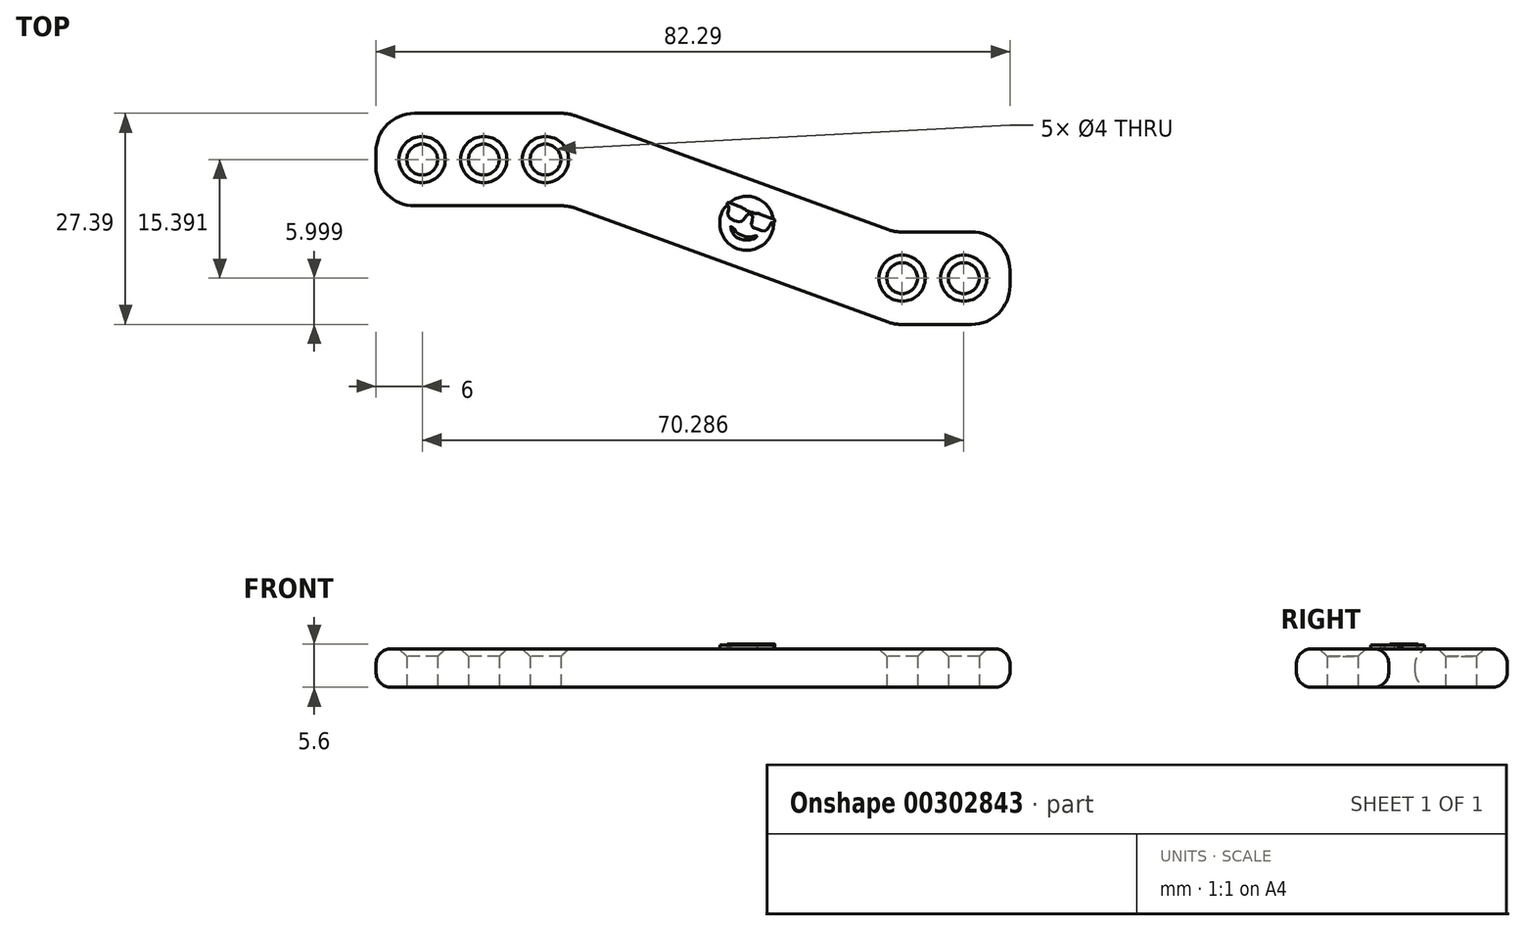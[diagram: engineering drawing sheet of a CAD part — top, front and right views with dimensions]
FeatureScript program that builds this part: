
annotation { "Feature Type Name" : "Feature", "Feature Type Description" : "" }
export const myFeature = defineFeature(function(context is Context, id is Id, definition is map)
    precondition{}
    {
        {
            var Q0;
            Q0=qCreatedBy(makeId("Top.planeOp"),FACE);
            var sketch = newSketch(context, id + "F0", { "sketchPlane" : qUnion([Q0])});
            skLineSegment(sketch, "E0.bottom", {"start": v(0, 0) * mm, "end": v(25, 0) * mm});
            skLineSegment(sketch, "E0.top", {"start": v(0, 12) * mm, "end": v(25, 12) * mm});
            skLineSegment(sketch, "E0.left", {"start": v(0, 0) * mm, "end": v(0, 12) * mm});
            skLineSegment(sketch, "E0.right", {"start": v(25, 0) * mm, "end": v(25, 12) * mm});
            skLineSegment(sketch, "E1", {"start": v(25, 12) * mm, "end": v(67.29, -3.4) * mm});
            skLineSegment(sketch, "E2", {"start": v(25, 0) * mm, "end": v(67.29, -15.4) * mm});
            skLineSegment(sketch, "E3", {"start": v(67.29, -3.4) * mm, "end": v(67.29, -15.4) * mm});
            skLineSegment(sketch, "E4.bottom", {"start": v(67.29, -3.4) * mm, "end": v(82.29, -3.4) * mm});
            skLineSegment(sketch, "E4.top", {"start": v(67.29, -15.4) * mm, "end": v(82.29, -15.4) * mm});
            skLineSegment(sketch, "E4.right", {"start": v(82.29, -3.4) * mm, "end": v(82.29, -15.4) * mm});
            skSolve(sketch);
        }
        {
            var Q0;
            Q0=makeQuery(id+"F0.imprint","IMPRINT",FACE,{"disambiguationData":[TD([[makeQuery(id+"F0.imprint","IMPRINT",EDGE,{"derivedFrom":sQuery(id+"F0.wireOp",EDGE,"E0.bottom")}),1.0]])]});
            var Q1;
            Q1=makeQuery(id+"F0.imprint","IMPRINT",FACE,{"disambiguationData":[TD([[makeQuery(id+"F0.imprint","IMPRINT",EDGE,{"derivedFrom":sQuery(id+"F0.wireOp",EDGE,"E0.right")}),-1.0]])]});
            var Q2;
            Q2=makeQuery(id+"F0.imprint","IMPRINT",FACE,{"disambiguationData":[TD([[makeQuery(id+"F0.imprint","IMPRINT",EDGE,{"derivedFrom":sQuery(id+"F0.wireOp",EDGE,"E4.bottom")}),-1.0]])]});
            extrude(context, id + "F1", {"entities" : qUnion([Q0, Q1, Q2]), "depth" : 5 * mm});
        }
        {
            var Q0;
            Q0=qCreatedBy(makeId("Top.planeOp"),FACE);
            var sketch = newSketch(context, id + "F2", { "sketchPlane" : qUnion([Q0])});
            skCircle(sketch, "E5", {"center": v(6, 6) * mm, "radius": 2 * mm});
            skCircle(sketch, "E6", {"center": v(76.29, -9.4) * mm, "radius": 2 * mm});
            skCircle(sketch, "E7.1.0.0", {"center": v(14, 6) * mm, "radius": 2 * mm});
            skCircle(sketch, "E7.2.0.0", {"center": v(22, 6) * mm, "radius": 2 * mm});
            skLineSegment(sketch, "E7.direction1", {"start": v(6, 6) * mm, "end": v(14, 6) * mm, "construction": true});
            skCircle(sketch, "E8.1.0.0", {"center": v(68.29, -9.4) * mm, "radius": 2 * mm});
            skLineSegment(sketch, "E8.direction1", {"start": v(76.29, -9.4) * mm, "end": v(68.29, -9.4) * mm, "construction": true});
            skSolve(sketch);
        }
        {
            var Q0;
            Q0 = qSketchRegion(id + "F2", true);
            extrude(context, id + "F3", {"entities" : qUnion([Q0]), "operationType" : NewBodyOperationType.REMOVE, "endBound" : BoundingType.THROUGH_ALL, "depth" : 25 * mm});
        }
        {
            var Q0;
            Q0=makeQuery(id+"F1.opExtrude","SWEPT_EDGE",EDGE,{"disambiguationData":[OSD([sQuery(id+"F0.wireOp",EDGE,"E0.top"),sQuery(id+"F0.wireOp",EDGE,"E0.left")])]});
            var Q1;
            Q1=makeQuery(id+"F1.opExtrude","SWEPT_EDGE",EDGE,{"disambiguationData":[OSD([sQuery(id+"F0.wireOp",EDGE,"E0.bottom"),sQuery(id+"F0.wireOp",EDGE,"E0.left")])]});
            var Q2;
            Q2=makeQuery(id+"F1.opExtrude","SWEPT_EDGE",EDGE,{"disambiguationData":[OSD([sQuery(id+"F0.wireOp",EDGE,"E4.bottom"),sQuery(id+"F0.wireOp",EDGE,"E4.right")])]});
            var Q3;
            Q3=makeQuery(id+"F1.opExtrude","SWEPT_EDGE",EDGE,{"disambiguationData":[OSD([sQuery(id+"F0.wireOp",EDGE,"E4.top"),sQuery(id+"F0.wireOp",EDGE,"E4.right")])]});
            var Q4;
            Q4=makeQuery(id+"F1.opExtrude","SWEPT_EDGE",EDGE,{"disambiguationData":[OSD([sQuery(id+"F0.wireOp",EDGE,"E0.top"),sQuery(id+"F0.wireOp",EDGE,"E0.right"),sQuery(id+"F0.wireOp",EDGE,"E1")])]});
            var Q5;
            Q5=makeQuery(id+"F1.opExtrude","SWEPT_EDGE",EDGE,{"disambiguationData":[OSD([sQuery(id+"F0.wireOp",EDGE,"E1"),sQuery(id+"F0.wireOp",EDGE,"E4.bottom"),sQuery(id+"F0.wireOp",EDGE,"E3")])]});
            var Q6;
            Q6=makeQuery(id+"F1.opExtrude","SWEPT_EDGE",EDGE,{"disambiguationData":[OSD([sQuery(id+"F0.wireOp",EDGE,"E2"),sQuery(id+"F0.wireOp",EDGE,"E4.top"),sQuery(id+"F0.wireOp",EDGE,"E3")])]});
            var Q7;
            Q7=makeQuery(id+"F1.opExtrude","SWEPT_EDGE",EDGE,{"disambiguationData":[OSD([sQuery(id+"F0.wireOp",EDGE,"E0.bottom"),sQuery(id+"F0.wireOp",EDGE,"E0.right"),sQuery(id+"F0.wireOp",EDGE,"E2")])]});
            fillet(context, id + "F4", {"entities" : qUnion([Q0, Q1, Q2, Q3, Q4, Q5, Q6, Q7]), "radius" : 5 * mm, "tangentPropagation" : true, "allowEdgeOverflow" : false});
        }
        {
            var Q0;
            Q0=makeQuery(id+"F1.opExtrude","CAP_EDGE",EDGE,{"disambiguationData":[OSD([sQuery(id+"F0.wireOp",EDGE,"E0.top")])],"isStart":false});
            var Q1;
            Q1=makeQuery(id+"F1.opExtrude","CAP_EDGE",EDGE,{"disambiguationData":[OSD([sQuery(id+"F0.wireOp",EDGE,"E0.bottom")])],"isStart":false});
            var Q2;
            Q2=makeQuery(id+"F1.opExtrude","CAP_EDGE",EDGE,{"disambiguationData":[OSD([sQuery(id+"F0.wireOp",EDGE,"E0.top")])],"isStart":true});
            var Q3;
            Q3=makeQuery(id+"F1.opExtrude","CAP_EDGE",EDGE,{"disambiguationData":[OSD([sQuery(id+"F0.wireOp",EDGE,"E0.bottom")])],"isStart":true});
            var Q4;
            Q4=makeQuery(id+"F1.opExtrude","CAP_EDGE",EDGE,{"disambiguationData":[OSD([sQuery(id+"F0.wireOp",EDGE,"E4.bottom")])],"isStart":false});
            var Q5;
            Q5=makeQuery(id+"F1.opExtrude","CAP_EDGE",EDGE,{"disambiguationData":[OSD([sQuery(id+"F0.wireOp",EDGE,"E4.top")])],"isStart":false});
            var Q6;
            Q6=makeQuery(id+"F1.opExtrude","CAP_EDGE",EDGE,{"disambiguationData":[OSD([sQuery(id+"F0.wireOp",EDGE,"E4.bottom")])],"isStart":true});
            var Q7;
            Q7=makeQuery(id+"F1.opExtrude","CAP_EDGE",EDGE,{"disambiguationData":[OSD([sQuery(id+"F0.wireOp",EDGE,"E4.top")])],"isStart":true});
            var Q8;
            Q8=makeQuery(id+"F1.opExtrude","CAP_EDGE",EDGE,{"disambiguationData":[OSD([sQuery(id+"F0.wireOp",EDGE,"E1")])],"isStart":false});
            var Q9;
            Q9=makeQuery(id+"F1.opExtrude","CAP_EDGE",EDGE,{"disambiguationData":[OSD([sQuery(id+"F0.wireOp",EDGE,"E1")])],"isStart":true});
            var Q10;
            Q10=makeQuery(id+"F1.opExtrude","CAP_EDGE",EDGE,{"disambiguationData":[OSD([sQuery(id+"F0.wireOp",EDGE,"E2")])],"isStart":true});
            var Q11;
            Q11=makeQuery(id+"F1.opExtrude","CAP_EDGE",EDGE,{"disambiguationData":[OSD([sQuery(id+"F0.wireOp",EDGE,"E2")])],"isStart":false});
            fillet(context, id + "F5", {"entities" : qUnion([Q0, Q1, Q2, Q3, Q4, Q5, Q6, Q7, Q8, Q9, Q10, Q11]), "radius" : 2 * mm, "tangentPropagation" : true, "allowEdgeOverflow" : false});
        }
        {
            var Q0;
            Q0=makeQuery(id+"F3.boolean.opBoolean","INTERSECT",EDGE,{"derivedFrom":[makeQuery(id+"F1.opExtrude","CAP_FACE",FACE,{"disambiguationData":[OSD([sQuery(id+"F0.wireOp",EDGE,"E0.bottom"),sQuery(id+"F0.wireOp",EDGE,"E0.top"),sQuery(id+"F0.wireOp",EDGE,"E0.left"),sQuery(id+"F0.wireOp",EDGE,"E1"),sQuery(id+"F0.wireOp",EDGE,"E2"),sQuery(id+"F0.wireOp",EDGE,"E4.bottom"),sQuery(id+"F0.wireOp",EDGE,"E4.top"),sQuery(id+"F0.wireOp",EDGE,"E4.right")])],"isStart":false}),makeQuery(id+"F3.opExtrude","SWEPT_FACE",FACE,{"disambiguationData":[OSD([sQuery(id+"F2.wireOp",EDGE,"E5")])]})]});
            var Q1;
            Q1=makeQuery(id+"F3.boolean.opBoolean","INTERSECT",EDGE,{"derivedFrom":[makeQuery(id+"F1.opExtrude","CAP_FACE",FACE,{"disambiguationData":[OSD([sQuery(id+"F0.wireOp",EDGE,"E0.bottom"),sQuery(id+"F0.wireOp",EDGE,"E0.top"),sQuery(id+"F0.wireOp",EDGE,"E0.left"),sQuery(id+"F0.wireOp",EDGE,"E1"),sQuery(id+"F0.wireOp",EDGE,"E2"),sQuery(id+"F0.wireOp",EDGE,"E4.bottom"),sQuery(id+"F0.wireOp",EDGE,"E4.top"),sQuery(id+"F0.wireOp",EDGE,"E4.right")])],"isStart":false}),makeQuery(id+"F3.opExtrude","SWEPT_FACE",FACE,{"disambiguationData":[OSD([sQuery(id+"F2.wireOp",EDGE,"E7.1.0.0")])]})]});
            var Q2;
            Q2=makeQuery(id+"F3.boolean.opBoolean","INTERSECT",EDGE,{"derivedFrom":[makeQuery(id+"F1.opExtrude","CAP_FACE",FACE,{"disambiguationData":[OSD([sQuery(id+"F0.wireOp",EDGE,"E0.bottom"),sQuery(id+"F0.wireOp",EDGE,"E0.top"),sQuery(id+"F0.wireOp",EDGE,"E0.left"),sQuery(id+"F0.wireOp",EDGE,"E1"),sQuery(id+"F0.wireOp",EDGE,"E2"),sQuery(id+"F0.wireOp",EDGE,"E4.bottom"),sQuery(id+"F0.wireOp",EDGE,"E4.top"),sQuery(id+"F0.wireOp",EDGE,"E4.right")])],"isStart":false}),makeQuery(id+"F3.opExtrude","SWEPT_FACE",FACE,{"disambiguationData":[OSD([sQuery(id+"F2.wireOp",EDGE,"E7.2.0.0")])]})]});
            var Q3;
            Q3=makeQuery(id+"F3.boolean.opBoolean","INTERSECT",EDGE,{"derivedFrom":[makeQuery(id+"F1.opExtrude","CAP_FACE",FACE,{"disambiguationData":[OSD([sQuery(id+"F0.wireOp",EDGE,"E0.bottom"),sQuery(id+"F0.wireOp",EDGE,"E0.top"),sQuery(id+"F0.wireOp",EDGE,"E0.left"),sQuery(id+"F0.wireOp",EDGE,"E1"),sQuery(id+"F0.wireOp",EDGE,"E2"),sQuery(id+"F0.wireOp",EDGE,"E4.bottom"),sQuery(id+"F0.wireOp",EDGE,"E4.top"),sQuery(id+"F0.wireOp",EDGE,"E4.right")])],"isStart":false}),makeQuery(id+"F3.opExtrude","SWEPT_FACE",FACE,{"disambiguationData":[OSD([sQuery(id+"F2.wireOp",EDGE,"E8.1.0.0")])]})]});
            var Q4;
            Q4=makeQuery(id+"F3.boolean.opBoolean","INTERSECT",EDGE,{"derivedFrom":[makeQuery(id+"F1.opExtrude","CAP_FACE",FACE,{"disambiguationData":[OSD([sQuery(id+"F0.wireOp",EDGE,"E0.bottom"),sQuery(id+"F0.wireOp",EDGE,"E0.top"),sQuery(id+"F0.wireOp",EDGE,"E0.left"),sQuery(id+"F0.wireOp",EDGE,"E1"),sQuery(id+"F0.wireOp",EDGE,"E2"),sQuery(id+"F0.wireOp",EDGE,"E4.bottom"),sQuery(id+"F0.wireOp",EDGE,"E4.top"),sQuery(id+"F0.wireOp",EDGE,"E4.right")])],"isStart":false}),makeQuery(id+"F3.opExtrude","SWEPT_FACE",FACE,{"disambiguationData":[OSD([sQuery(id+"F2.wireOp",EDGE,"E6")])]})]});
            chamfer(context, id + "F6", {"entities" : qUnion([Q0, Q1, Q2, Q3, Q4]), "width" : 1 * mm, "tangentPropagation" : true});
        }
        {
            var Q0;
            Q0=makeQuery(id+"F1.opExtrude","CAP_FACE",FACE,{"disambiguationData":[OSD([sQuery(id+"F0.wireOp",EDGE,"E0.bottom"),sQuery(id+"F0.wireOp",EDGE,"E0.top"),sQuery(id+"F0.wireOp",EDGE,"E0.left"),sQuery(id+"F0.wireOp",EDGE,"E1"),sQuery(id+"F0.wireOp",EDGE,"E2"),sQuery(id+"F0.wireOp",EDGE,"E4.bottom"),sQuery(id+"F0.wireOp",EDGE,"E4.top"),sQuery(id+"F0.wireOp",EDGE,"E4.right")])],"isStart":false});
            var sketch = newSketch(context, id + "F7", { "sketchPlane" : qUnion([Q0])});
            skArc(sketch, "E9", {"start": v(45.57, 0.14) * mm, "mid": v(46.88, -5.54) * mm, "end": v(51.6, -2.13) * mm});
            skFitSpline(sketch, "E10", {"points": [v(45.66, 0.42) * mm, v(45.84, 0.4) * mm, v(45.98, 0.35) * mm, v(46.2, 0.27) * mm, v(46.38, 0.22) * mm, v(46.53, 0.17) * mm, v(46.67, 0.12) * mm, v(46.93, 0) * mm, v(47.32, -0.16) * mm, v(47.58, -0.28) * mm, v(47.8, -0.4) * mm, v(48.05, -0.58) * mm, v(48.3, -0.7) * mm, v(48.8, -0.84) * mm, v(49.19, -1.01) * mm, v(49.58, -1) * mm, v(49.86, -1.1) * mm, v(50.46, -1.31) * mm, v(51.12, -1.57) * mm, v(51.56, -1.67) * mm, v(51.72, -1.79) * mm, v(51.75, -2.06) * mm, v(51.4, -2.17) * mm, v(51.28, -2.24) * mm, v(51.01, -2.7) * mm, v(50.63, -3.18) * mm, v(50.29, -3.26) * mm, v(49.65, -3.1) * mm, v(48.86, -2.73) * mm, v(48.74, -2.24) * mm, v(48.9, -1.42) * mm, v(48.78, -1.2) * mm, v(48.38, -1.03) * mm, v(48.22, -1.08) * mm, v(47.79, -1.71) * mm, v(47.55, -1.92) * mm, v(47.3, -2.04) * mm, v(46.83, -2.02) * mm, v(45.9, -1.6) * mm, v(45.72, -1.32) * mm, v(45.66, -0.83) * mm, v(45.84, -0.32) * mm, v(45.72, 0) * mm, v(45.57, 0.14) * mm, v(45.66, 0.42) * mm]});
            skFitSpline(sketch, "E11", {"points": [v(46.06, -2.67) * mm, v(46.26, -2.78) * mm, v(46.39, -2.95) * mm, v(46.57, -3.18) * mm, v(46.88, -3.51) * mm, v(47.13, -3.7) * mm, v(47.41, -3.82) * mm, v(47.73, -3.94) * mm, v(48.04, -4.04) * mm, v(48.34, -4.05) * mm, v(48.76, -4) * mm, v(49.04, -3.95) * mm, v(49.34, -3.9) * mm, v(49.45, -3.97) * mm, v(49.22, -4.15) * mm, v(48.9, -4.3) * mm, v(48.3, -4.43) * mm, v(47.85, -4.44) * mm, v(47.26, -4.3) * mm, v(46.68, -4) * mm, v(46.34, -3.57) * mm, v(46.08, -3.03) * mm, v(46.06, -2.67) * mm]});
            skArc(sketch, "E12.trimOffspring", {"start": v(51.56, -1.67) * mm, "mid": v(49.3, 1.03) * mm, "end": v(45.84, 0.4) * mm});
            skSolve(sketch);
        }
        {
            var Q0;
            {var subQ0=sQuery(id+"F7.wireOp",EDGE,"E12.trimOffspring");var subQ1=sQuery(id+"F7.wireOp",EDGE,"E10");var subQ2=makeQuery(id+"F7.imprint","INTERSECT",VERTEX,{"disambiguationData":[OD(0.0)],"derivedFrom":[subQ1,subQ0]});Q0=makeQuery(id+"F7.imprint","IMPRINT",FACE,{"disambiguationData":[TD([[makeQuery(id+"F7.imprint","IMPRINT",EDGE,{"disambiguationData":[TD([[subQ2,1.0]])],"derivedFrom":subQ1}),-1.0]])]});}
            extrude(context, id + "F8", {"entities" : qUnion([Q0]), "operationType" : NewBodyOperationType.ADD, "depth" : 0.6 * mm});
        }
        {
            var Q0;
            {var subQ0=sQuery(id+"F7.wireOp",EDGE,"E12.trimOffspring");var subQ1=sQuery(id+"F7.wireOp",EDGE,"E10");var subQ2=makeQuery(id+"F7.imprint","INTERSECT",VERTEX,{"disambiguationData":[OD(0.0)],"derivedFrom":[subQ1,subQ0]});Q0=makeQuery(id+"F7.imprint","IMPRINT",FACE,{"disambiguationData":[TD([[makeQuery(id+"F7.imprint","IMPRINT",EDGE,{"disambiguationData":[TD([[subQ2,1.0]])],"derivedFrom":subQ1}),1.0]])]});}
            var Q1;
            {var subQ0=sQuery(id+"F7.wireOp",EDGE,"E9");Q1=makeQuery(id+"F7.imprint","IMPRINT",FACE,{"disambiguationData":[TD([[makeQuery(id+"F7.imprint","IMPRINT",EDGE,{"derivedFrom":subQ0}),1.0]])]});}
            extrude(context, id + "F9", {"entities" : qUnion([Q0, Q1]), "operationType" : NewBodyOperationType.ADD, "depth" : 0.5 * mm});
        }
    });
